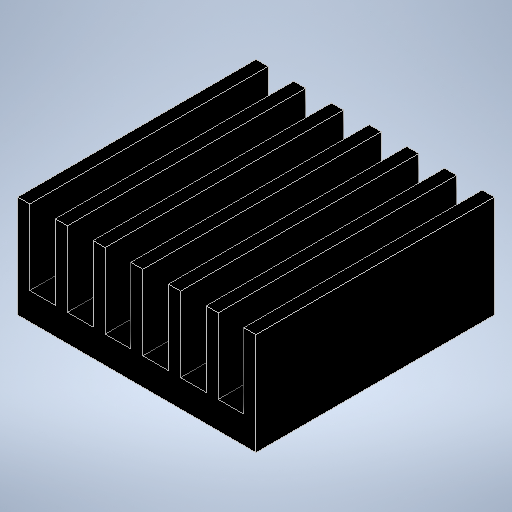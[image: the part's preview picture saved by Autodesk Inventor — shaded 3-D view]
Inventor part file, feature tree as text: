
AUTODESK INVENTOR PART (.ipt)
format: ipt  version: 2025 (Build 290162000, 162)  size: 274,944 bytes
history: native  units: mm
features: extrude x2, sketch x2, projected_geometry x1
ambient origin geometry x8: Origin, YZ Plane, XZ Plane, XY Plane, X Axis, Y Axis, Z Axis, Center Point
bodies: Solid1 (feature_tree)
feature tree (5):
  extrude  "Extrusion1"  Depth=14.0mm
  extrude  "Extrusion2"  Depth=6.0mm
  sketch  "Sketch1"  dims[d0=14.0mm d1=14.0mm]
  sketch  "Sketch2"  dims[d2=6.0mm d3=0.0mm d4=6.0mm d5=1.6mm d6=1.5mm d8=1.5mm d9=1.5mm d10=1.5mm d11=1.5mm d12=1.5mm d13=0.0mm d14=0.0mm]
  projected_geometry  "Projected Loop1"
